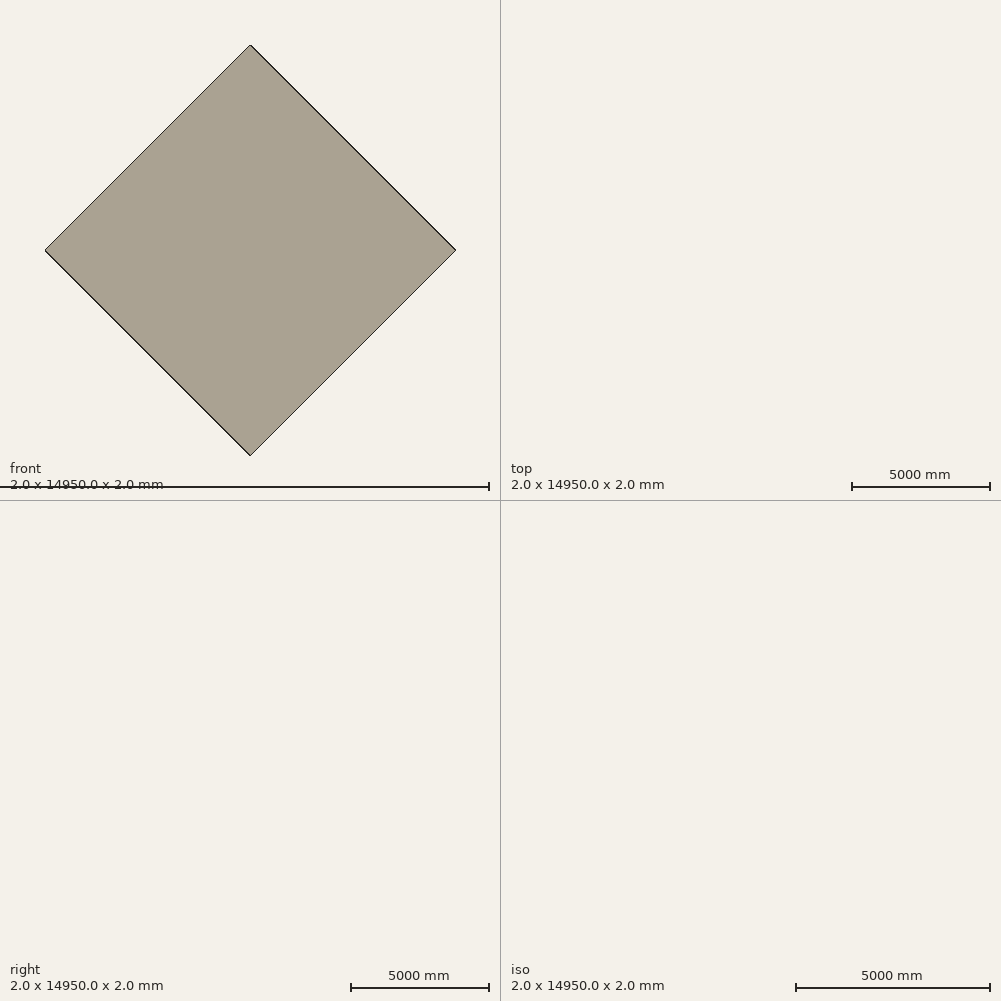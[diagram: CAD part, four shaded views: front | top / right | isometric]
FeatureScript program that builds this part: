
annotation { "Feature Type Name" : "Feature", "Feature Type Description" : "" }
export const myFeature = defineFeature(function(context is Context, id is Id, definition is map)
    precondition{}
    {
        {
            assignVariable(context, id + "F0", {"name" : "l", "anyValue" : 14950});
        }
        {
            var Q0;
            Q0=qCreatedBy(makeId("Front.planeOp"),FACE);
            var sketch = newSketch(context, id + "F1", { "sketchPlane" : qUnion([Q0])});
            skCircle(sketch, "E0", {"center": v(0, 0) * mm, "radius": 1 * mm});
            skSolve(sketch);
        }
        {
            var Q0;
            Q0=qSketchRegion(id+"F1",true);
            extrude(context, id + "F2", {"entities" : qUnion([Q0]), "depth" : (getVariable(context, 'l')) * mm, "offsetDistance" : 25 * mm});
        }
    });
